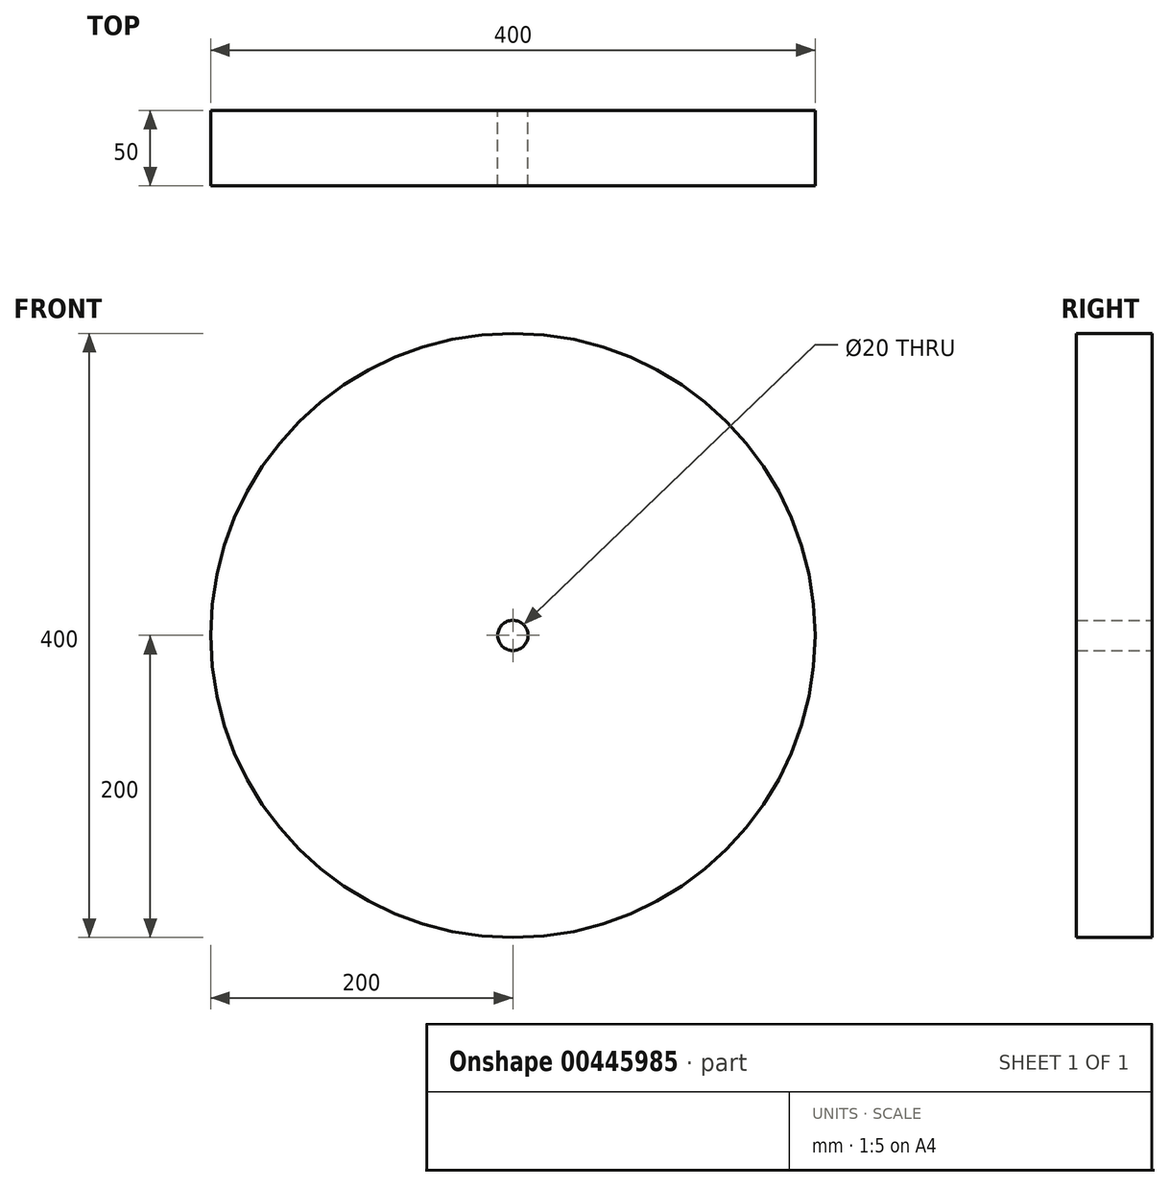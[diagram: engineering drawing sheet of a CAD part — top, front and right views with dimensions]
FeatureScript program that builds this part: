
annotation { "Feature Type Name" : "Feature", "Feature Type Description" : "" }
export const myFeature = defineFeature(function(context is Context, id is Id, definition is map)
    precondition{}
    {
        {
            var Q0;
            Q0=qCreatedBy(makeId("Front.planeOp"),FACE);
            var sketch = newSketch(context, id + "F0", { "sketchPlane" : qUnion([Q0])});
            skCircle(sketch, "E0", {"center": v(0, 0) * mm, "radius": 200 * mm});
            skCircle(sketch, "E1", {"center": v(0, 0) * mm, "radius": 10 * mm});
            skSolve(sketch);
        }
        {
            var Q0;
            Q0 = qSketchRegion(id + "F0", true);
            var Q1;
            Q1=makeQuery(id+"F0.imprint","IMPRINT",FACE,{"disambiguationData":[TD([[makeQuery(id+"F0.imprint","IMPRINT",EDGE,{"derivedFrom":sQuery(id+"F0.wireOp",EDGE,"E0")}),1.0]])]});
            extrude(context, id + "F1", {"entities" : qUnion([Q0, Q1]), "depth" : 50 * mm});
        }
    });
